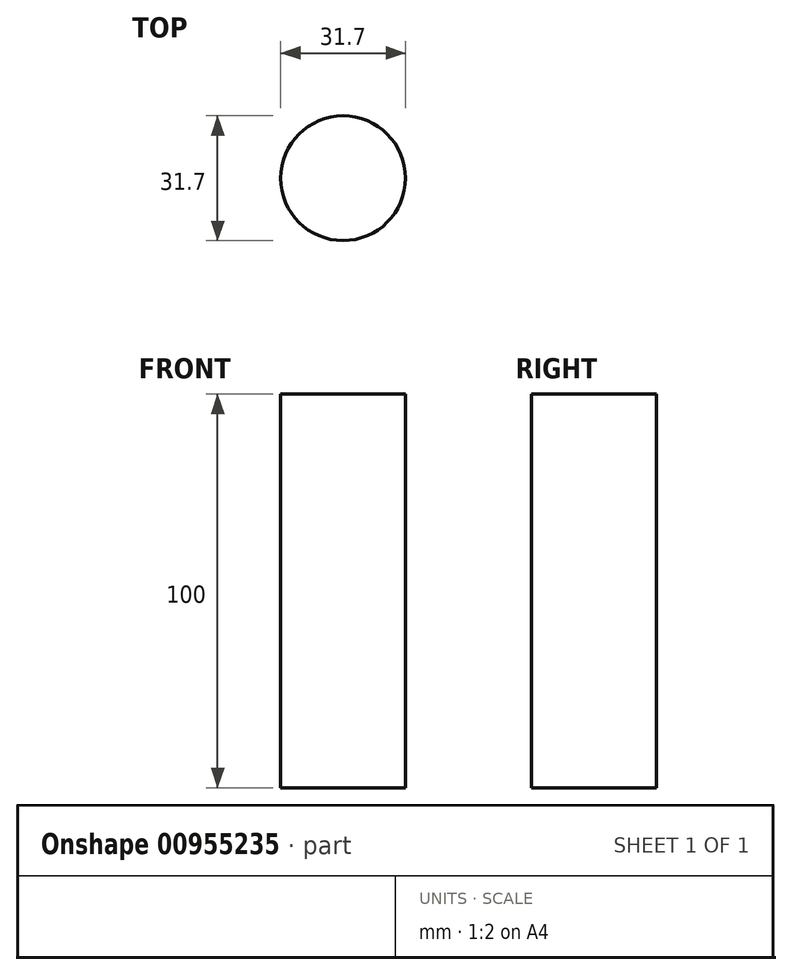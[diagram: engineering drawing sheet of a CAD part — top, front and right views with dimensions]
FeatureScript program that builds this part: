
annotation { "Feature Type Name" : "Feature", "Feature Type Description" : "" }
export const myFeature = defineFeature(function(context is Context, id is Id, definition is map)
    precondition{}
    {
        {
            var Q0;
            Q0=qCreatedBy(makeId("Top.planeOp"),FACE);
            var sketch = newSketch(context, id + "F0", { "sketchPlane" : qUnion([Q0])});
            skCircle(sketch, "E0", {"center": v(0, 0) * mm, "radius": 15.85 * mm});
            skSolve(sketch);
        }
        {
            var Q0;
            Q0=makeQuery(id+"F0.imprint","IMPRINT",FACE,{"disambiguationData":[TD([[makeQuery(id+"F0.imprint","IMPRINT",EDGE,{"derivedFrom":sQuery(id+"F0.wireOp",EDGE,"E0")}),1.0]])]});
            var Q1;
            Q1=sQuery(id+"F0.wireOp",EDGE,"E0");
            extrude(context, id + "F1", {"entities" : qUnion([Q0]), "bodyType" : ToolBodyType.SURFACE, "surfaceEntities" : qUnion([Q1]), "endBound" : BoundingType.SYMMETRIC, "depth" : 100 * mm, "offsetDistance" : 25 * mm});
        }
        {
            var Q0;
            Q0=qCreatedBy(makeId("Right.planeOp"),FACE);
            cPlane(context, id + "F2", {"entities" : qUnion([Q0]), "cplaneType" : CPlaneType.OFFSET, "offset" : 25 * mm, "width" : 150 * mm, "height" : 150 * mm});
        }
    });
